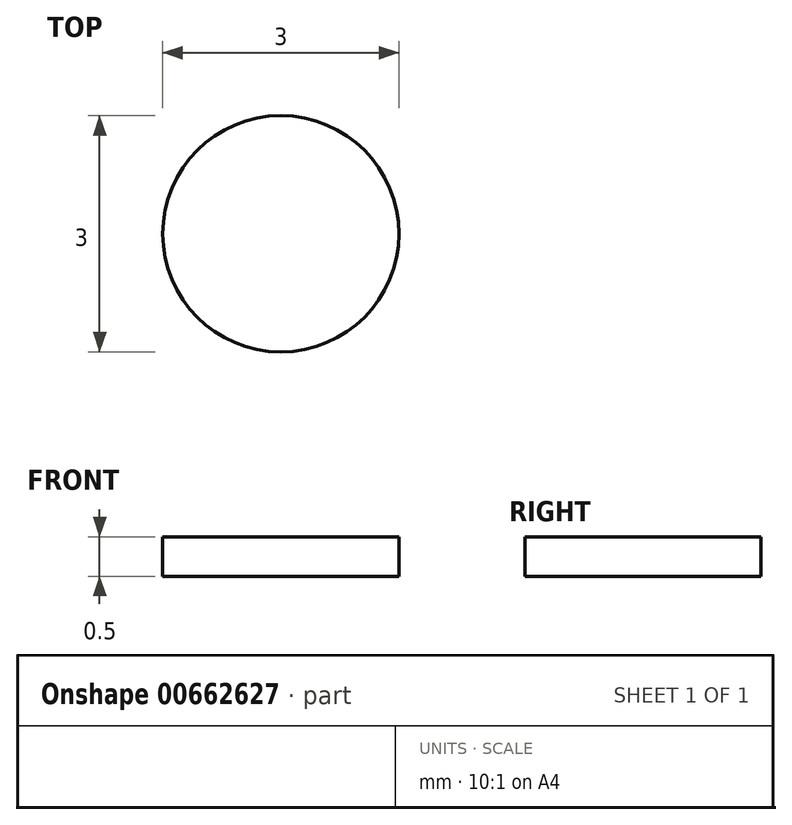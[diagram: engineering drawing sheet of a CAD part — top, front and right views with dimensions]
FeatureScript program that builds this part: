
annotation { "Feature Type Name" : "Feature", "Feature Type Description" : "" }
export const myFeature = defineFeature(function(context is Context, id is Id, definition is map)
    precondition{}
    {
        {
            var Q0;
            Q0=qCreatedBy(makeId("Top.planeOp"),FACE);
            var sketch = newSketch(context, id + "F0", { "sketchPlane" : qUnion([Q0])});
            skCircle(sketch, "E0", {"center": v(0, 0) * mm, "radius": 1.5 * mm});
            skSolve(sketch);
        }
        {
            var Q0;
            Q0=makeQuery(id+"F0.imprint","IMPRINT",FACE,{"disambiguationData":[TD([[makeQuery(id+"F0.imprint","IMPRINT",EDGE,{"derivedFrom":sQuery(id+"F0.wireOp",EDGE,"E0")}),1.0]])]});
            extrude(context, id + "F1", {"entities" : qUnion([Q0]), "depth" : .5 * mm, "offsetDistance" : 25 * mm});
        }
    });
